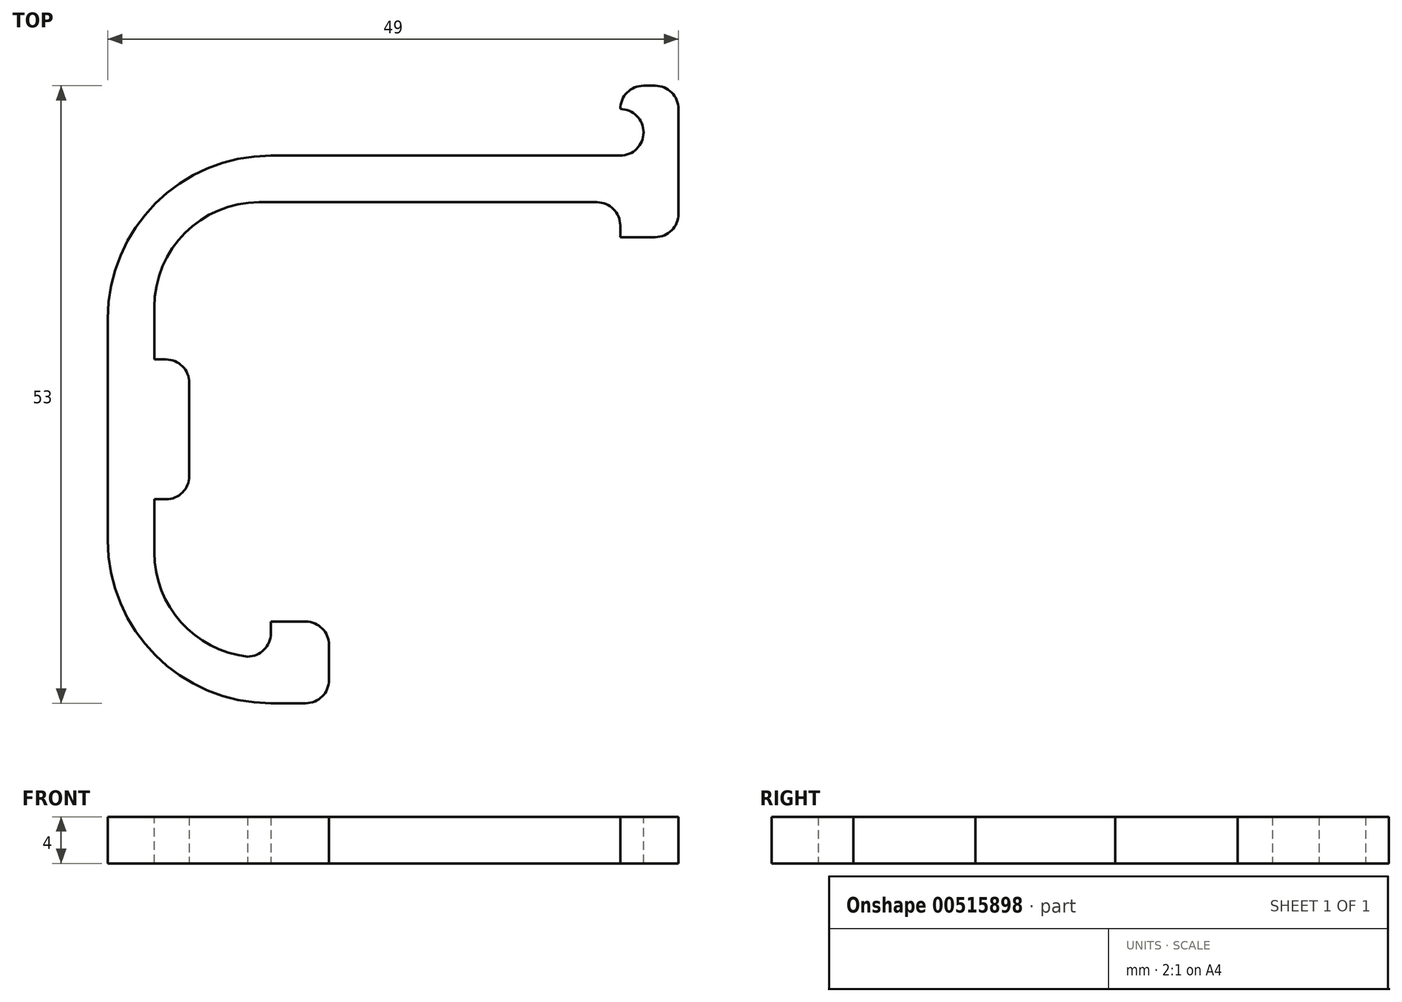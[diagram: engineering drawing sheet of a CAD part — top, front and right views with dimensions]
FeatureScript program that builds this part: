
annotation { "Feature Type Name" : "Feature", "Feature Type Description" : "" }
export const myFeature = defineFeature(function(context is Context, id is Id, definition is map)
    precondition{}
    {
        {
            var Q0;
            Q0=qCreatedBy(makeId("Top.planeOp"),FACE);
            var sketch = newSketch(context, id + "F0", { "sketchPlane" : qUnion([Q0])});
            skLineSegment(sketch, "E0.bottom", {"start": v(20.32, 23.5) * mm, "end": v(121.92, 23.5) * mm, "construction": true});
            skLineSegment(sketch, "E0.top", {"start": v(20.32, 56.5) * mm, "end": v(121.92, 56.5) * mm, "construction": true});
            skLineSegment(sketch, "E0.left", {"start": v(20.32, 23.5) * mm, "end": v(20.32, 56.5) * mm, "construction": true});
            skLineSegment(sketch, "E0.right", {"start": v(121.92, 23.5) * mm, "end": v(121.92, 56.5) * mm, "construction": true});
            skLineSegment(sketch, "E1.bottom", {"start": v(0, 0) * mm, "end": v(80, 0) * mm, "construction": true});
            skLineSegment(sketch, "E1.top", {"start": v(0, 80) * mm, "end": v(80, 80) * mm, "construction": true});
            skLineSegment(sketch, "E1.left", {"start": v(0, 0) * mm, "end": v(0, 80) * mm, "construction": true});
            skLineSegment(sketch, "E1.right", {"start": v(80, 0) * mm, "end": v(80, 80) * mm, "construction": true});
            skLineSegment(sketch, "E2", {"start": v(27.32, 23.5) * mm, "end": v(32.32, 23.5) * mm});
            skLineSegment(sketch, "E3", {"start": v(32.32, 23.5) * mm, "end": v(32.32, 16.5) * mm});
            skLineSegment(sketch, "E4", {"start": v(32.32, 16.5) * mm, "end": v(13.32, 16.5) * mm});
            skLineSegment(sketch, "E5", {"start": v(13.32, 16.5) * mm, "end": v(13.32, 63.5) * mm});
            skLineSegment(sketch, "E6", {"start": v(13.32, 63.5) * mm, "end": v(59.32, 63.5) * mm});
            skLineSegment(sketch, "E7", {"start": v(59.32, 63.5) * mm, "end": v(59.32, 67.5) * mm});
            skLineSegment(sketch, "E8", {"start": v(59.32, 67.5) * mm, "end": v(57.32, 67.5) * mm});
            skLineSegment(sketch, "E9", {"start": v(57.32, 67.5) * mm, "end": v(57.32, 69.5) * mm});
            skLineSegment(sketch, "E10", {"start": v(57.32, 69.5) * mm, "end": v(62.32, 69.5) * mm});
            skLineSegment(sketch, "E11", {"start": v(62.32, 69.5) * mm, "end": v(62.32, 56.5) * mm});
            skLineSegment(sketch, "E12", {"start": v(62.32, 56.5) * mm, "end": v(57.32, 56.5) * mm});
            skLineSegment(sketch, "E13", {"start": v(57.32, 56.5) * mm, "end": v(57.32, 59.5) * mm});
            skLineSegment(sketch, "E14", {"start": v(57.32, 59.5) * mm, "end": v(17.32, 59.5) * mm});
            skLineSegment(sketch, "E15", {"start": v(17.32, 59.5) * mm, "end": v(17.32, 46) * mm});
            skLineSegment(sketch, "E16", {"start": v(17.32, 20.5) * mm, "end": v(27.32, 20.5) * mm});
            skLineSegment(sketch, "E17", {"start": v(27.32, 20.5) * mm, "end": v(27.32, 23.5) * mm});
            skLineSegment(sketch, "E18.bottom", {"start": v(17.32, 46) * mm, "end": v(20.32, 46) * mm});
            skLineSegment(sketch, "E18.top", {"start": v(17.32, 34) * mm, "end": v(20.32, 34) * mm});
            skLineSegment(sketch, "E18.right", {"start": v(20.32, 46) * mm, "end": v(20.32, 34) * mm});
            skLineSegment(sketch, "E19.trimOffspring", {"start": v(17.32, 34) * mm, "end": v(17.32, 20.5) * mm});
            skSolve(sketch);
        }
        {
            var Q0;
            Q0 = qSketchRegion(id + "F0", true);
            extrude(context, id + "F1", {"entities" : qUnion([Q0]), "depth" : 4 * mm, "offsetDistance" : 25 * mm});
        }
        {
            var Q0;
            Q0=makeQuery(id+"F1.opExtrude","SWEPT_EDGE",EDGE,{"disambiguationData":[OSD([sQuery(id+"F0.wireOp",EDGE,"E6"),sQuery(id+"F0.wireOp",EDGE,"E7")])]});
            var Q1;
            Q1=makeQuery(id+"F1.opExtrude","SWEPT_EDGE",EDGE,{"disambiguationData":[OSD([sQuery(id+"F0.wireOp",EDGE,"E7"),sQuery(id+"F0.wireOp",EDGE,"E8")])]});
            var Q2;
            Q2=makeQuery(id+"F1.opExtrude","SWEPT_EDGE",EDGE,{"disambiguationData":[OSD([sQuery(id+"F0.wireOp",EDGE,"E13"),sQuery(id+"F0.wireOp",EDGE,"E14")])]});
            var Q3;
            Q3=makeQuery(id+"F1.opExtrude","SWEPT_EDGE",EDGE,{"disambiguationData":[OSD([sQuery(id+"F0.wireOp",EDGE,"E9"),sQuery(id+"F0.wireOp",EDGE,"E10")])]});
            var Q4;
            Q4=makeQuery(id+"F1.opExtrude","SWEPT_EDGE",EDGE,{"disambiguationData":[OSD([sQuery(id+"F0.wireOp",EDGE,"E10"),sQuery(id+"F0.wireOp",EDGE,"E11")])]});
            var Q5;
            Q5=makeQuery(id+"F1.opExtrude","SWEPT_EDGE",EDGE,{"disambiguationData":[OSD([sQuery(id+"F0.wireOp",EDGE,"E11"),sQuery(id+"F0.wireOp",EDGE,"E12")])]});
            var Q6;
            Q6=makeQuery(id+"F1.opExtrude","SWEPT_EDGE",EDGE,{"disambiguationData":[OSD([sQuery(id+"F0.wireOp",EDGE,"E18.bottom"),sQuery(id+"F0.wireOp",EDGE,"E18.right")])]});
            var Q7;
            Q7=makeQuery(id+"F1.opExtrude","SWEPT_EDGE",EDGE,{"disambiguationData":[OSD([sQuery(id+"F0.wireOp",EDGE,"E18.top"),sQuery(id+"F0.wireOp",EDGE,"E18.right")])]});
            var Q8;
            Q8=makeQuery(id+"F1.opExtrude","SWEPT_EDGE",EDGE,{"disambiguationData":[OSD([sQuery(id+"F0.wireOp",EDGE,"E16"),sQuery(id+"F0.wireOp",EDGE,"E17")])]});
            var Q9;
            Q9=makeQuery(id+"F1.opExtrude","SWEPT_EDGE",EDGE,{"disambiguationData":[OSD([sQuery(id+"F0.wireOp",EDGE,"E3"),sQuery(id+"F0.wireOp",EDGE,"E4")])]});
            var Q10;
            Q10=makeQuery(id+"F1.opExtrude","SWEPT_EDGE",EDGE,{"disambiguationData":[OSD([sQuery(id+"F0.wireOp",EDGE,"E2"),sQuery(id+"F0.wireOp",EDGE,"E3")])]});
            fillet(context, id + "F2", {"entities" : qUnion([Q0, Q1, Q2, Q3, Q4, Q5, Q6, Q7, Q8, Q9, Q10]), "radius" : 2 * mm, "tangentPropagation" : true, "allowEdgeOverflow" : false});
        }
        {
            var Q0;
            Q0=makeQuery(id+"F1.opExtrude","SWEPT_EDGE",EDGE,{"disambiguationData":[OSD([sQuery(id+"F0.wireOp",EDGE,"E14"),sQuery(id+"F0.wireOp",EDGE,"E15")])]});
            var Q1;
            Q1=makeQuery(id+"F1.opExtrude","SWEPT_EDGE",EDGE,{"disambiguationData":[OSD([sQuery(id+"F0.wireOp",EDGE,"E16"),sQuery(id+"F0.wireOp",EDGE,"E19.trimOffspring")])]});
            fillet(context, id + "F3", {"entities" : qUnion([Q0, Q1]), "radius" : 9 * mm, "tangentPropagation" : true, "allowEdgeOverflow" : false});
        }
        {
            var Q0;
            Q0=makeQuery(id+"F1.opExtrude","SWEPT_EDGE",EDGE,{"disambiguationData":[OSD([sQuery(id+"F0.wireOp",EDGE,"E5"),sQuery(id+"F0.wireOp",EDGE,"E6")])]});
            var Q1;
            Q1=makeQuery(id+"F1.opExtrude","SWEPT_EDGE",EDGE,{"disambiguationData":[OSD([sQuery(id+"F0.wireOp",EDGE,"E4"),sQuery(id+"F0.wireOp",EDGE,"E5")])]});
            fillet(context, id + "F4", {"entities" : qUnion([Q0, Q1]), "radius" : 14 * mm, "tangentPropagation" : true, "allowEdgeOverflow" : false});
        }
    });
